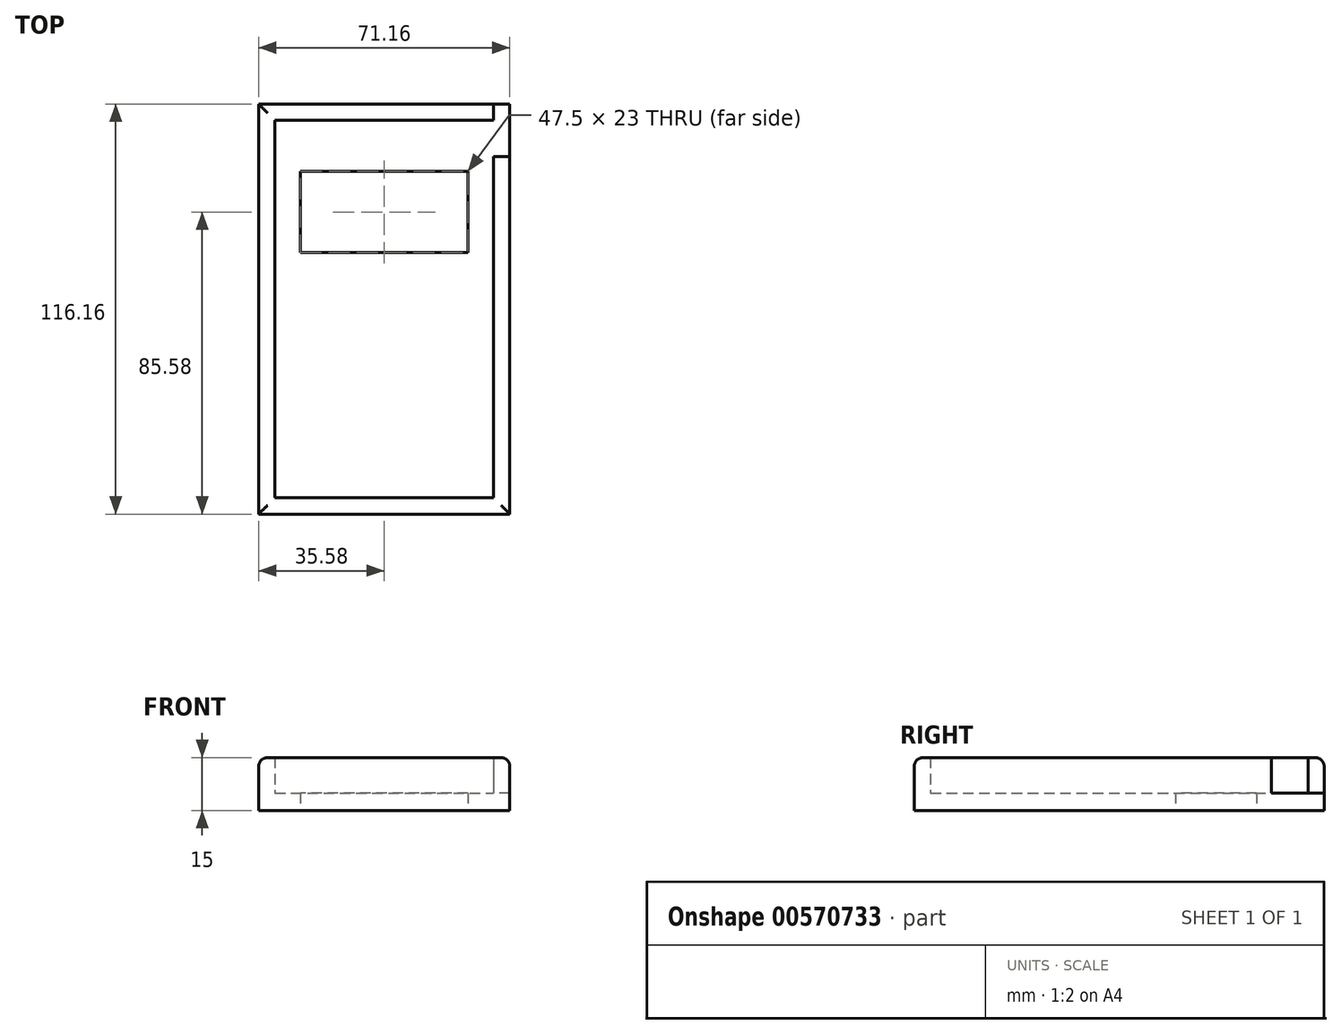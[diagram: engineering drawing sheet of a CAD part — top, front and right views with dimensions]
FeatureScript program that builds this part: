
annotation { "Feature Type Name" : "Feature", "Feature Type Description" : "" }
export const myFeature = defineFeature(function(context is Context, id is Id, definition is map)
    precondition{}
    {
        {
            var Q0;
            Q0=qCreatedBy(makeId("Top.planeOp"),FACE);
            var sketch = newSketch(context, id + "F0", { "sketchPlane" : qUnion([Q0])});
            skLineSegment(sketch, "E0.bottom", {"start": v(35.58, 58.08) * mm, "end": v(-35.58, 58.08) * mm});
            skLineSegment(sketch, "E0.top", {"start": v(35.58, -58.08) * mm, "end": v(-35.58, -58.08) * mm});
            skLineSegment(sketch, "E0.right", {"start": v(-35.58, 58.08) * mm, "end": v(-35.58, -58.08) * mm});
            skPoint(sketch, "E0.middle", {"position": v(0, 0) * mm});
            skLineSegment(sketch, "E1.bottom", {"start": v(26.99, 41.5) * mm, "end": v(-26.99, 41.5) * mm, "construction": true});
            skLineSegment(sketch, "E1.top", {"start": v(26.99, 16.1) * mm, "end": v(-26.99, 16.1) * mm, "construction": true});
            skLineSegment(sketch, "E1.left", {"start": v(26.99, 41.5) * mm, "end": v(26.99, 16.1) * mm, "construction": true});
            skLineSegment(sketch, "E1.right", {"start": v(-26.99, 41.5) * mm, "end": v(-26.99, 16.1) * mm, "construction": true});
            skPoint(sketch, "E1.middle", {"position": v(0, 28.8) * mm});
            skLineSegment(sketch, "E2.trimOffspring", {"start": v(35.58, 43.7) * mm, "end": v(35.58, -58.08) * mm});
            skLineSegment(sketch, "E3.bottom", {"start": v(30, 52.5) * mm, "end": v(-30, 52.5) * mm, "construction": true});
            skLineSegment(sketch, "E3.top", {"start": v(30, -52.5) * mm, "end": v(-30, -52.5) * mm, "construction": true});
            skLineSegment(sketch, "E3.left", {"start": v(30, 52.5) * mm, "end": v(30, -52.5) * mm, "construction": true});
            skLineSegment(sketch, "E3.right", {"start": v(-30, 52.5) * mm, "end": v(-30, -52.5) * mm, "construction": true});
            skLineSegment(sketch, "E4", {"start": v(35.58, 58.08) * mm, "end": v(35.58, 43.7) * mm});
            skLineSegment(sketch, "E5.0", {"start": v(31, 53.5) * mm, "end": v(-31, 53.5) * mm});
            skLineSegment(sketch, "E5.1", {"start": v(31, 53.5) * mm, "end": v(31, -53.5) * mm});
            skLineSegment(sketch, "E5.2", {"start": v(31, -53.5) * mm, "end": v(-31, -53.5) * mm});
            skLineSegment(sketch, "E5.3", {"start": v(-31, 53.5) * mm, "end": v(-31, -53.5) * mm});
            skLineSegment(sketch, "E6", {"start": v(31, 43.15) * mm, "end": v(35.58, 43.15) * mm});
            skLineSegment(sketch, "E7.bottom", {"start": v(23.75, 39) * mm, "end": v(-23.75, 39) * mm});
            skLineSegment(sketch, "E7.top", {"start": v(23.75, 16) * mm, "end": v(-23.75, 16) * mm});
            skLineSegment(sketch, "E7.left", {"start": v(23.75, 39) * mm, "end": v(23.75, 16) * mm});
            skLineSegment(sketch, "E7.right", {"start": v(-23.75, 39) * mm, "end": v(-23.75, 16) * mm});
            skPoint(sketch, "E7.middle", {"position": v(0, 27.5) * mm});
            skLineSegment(sketch, "E8", {"start": v(31, 53.5) * mm, "end": v(31, 58.08) * mm});
            skSolve(sketch);
        }
        {
            var Q0;
            {var subQ3=sQuery(id+"F0.wireOp",EDGE,"E4");Q0=makeQuery(id+"F0.imprint","IMPRINT",FACE,{"disambiguationData":[TD([[makeQuery(id+"F0.imprint","IMPRINT",EDGE,{"derivedFrom":subQ3}),-1.0]])]});}
            var Q1;
            {var subQ1=sQuery(id+"F0.wireOp",EDGE,"E0.top");Q1=makeQuery(id+"F0.imprint","IMPRINT",FACE,{"disambiguationData":[TD([[makeQuery(id+"F0.imprint","IMPRINT",EDGE,{"derivedFrom":subQ1}),-1.0]])]});}
            var Q2;
            {var subQ3=sQuery(id+"F0.wireOp",EDGE,"E5.0");Q2=makeQuery(id+"F0.imprint","IMPRINT",FACE,{"disambiguationData":[TD([[makeQuery(id+"F0.imprint","IMPRINT",EDGE,{"derivedFrom":subQ3}),1.0]])]});}
            extrude(context, id + "F1", {"entities" : qUnion([Q0, Q1, Q2]), "depth" : 5 * mm, "offsetDistance" : 25 * mm});
        }
        {
            var Q0;
            {var subQ1=sQuery(id+"F0.wireOp",EDGE,"E0.top");Q0=makeQuery(id+"F0.imprint","IMPRINT",FACE,{"disambiguationData":[TD([[makeQuery(id+"F0.imprint","IMPRINT",EDGE,{"derivedFrom":subQ1}),-1.0]])]});}
            extrude(context, id + "F2", {"entities" : qUnion([Q0]), "operationType" : NewBodyOperationType.ADD, "depth" : 15 * mm, "offsetDistance" : 25 * mm});
        }
        {
            var Q0;
            Q0=makeQuery(id+"F2.opExtrude","CAP_EDGE",EDGE,{"disambiguationData":[OSD([sQuery(id+"F0.wireOp",EDGE,"E0.right")])],"isStart":false});
            var Q1;
            Q1=makeQuery(id+"F2.opExtrude","CAP_EDGE",EDGE,{"disambiguationData":[OSD([sQuery(id+"F0.wireOp",EDGE,"E0.bottom")])],"isStart":false});
            var Q2;
            Q2=makeQuery(id+"F2.opExtrude","CAP_EDGE",EDGE,{"disambiguationData":[OSD([sQuery(id+"F0.wireOp",EDGE,"E0.top")])],"isStart":false});
            var Q3;
            Q3=makeQuery(id+"F2.opExtrude","CAP_EDGE",EDGE,{"disambiguationData":[OSD([sQuery(id+"F0.wireOp",EDGE,"E2.trimOffspring")])],"isStart":false});
            var Q4;
            Q4=makeQuery(id+"F2.opExtrude","CAP_EDGE",EDGE,{"disambiguationData":[OSD([sQuery(id+"F0.wireOp",EDGE,"E4")])],"isStart":false});
            fillet(context, id + "F3", {"entities" : qUnion([Q0, Q1, Q2, Q3, Q4]), "radius" : 2.5 * mm, "tangentPropagation" : true, "allowEdgeOverflow" : false});
        }
    });
